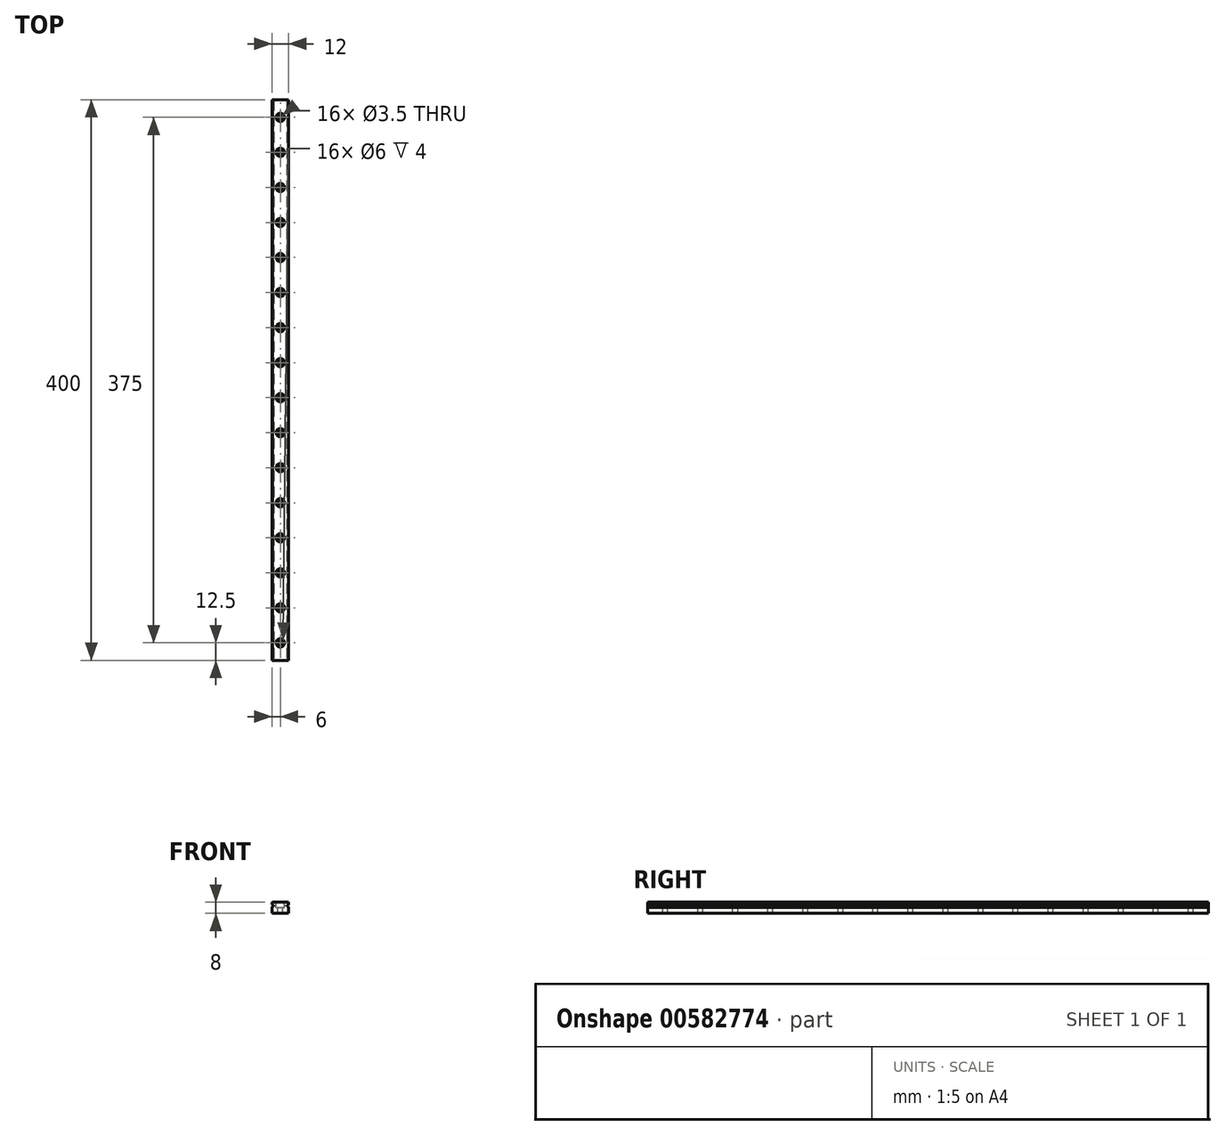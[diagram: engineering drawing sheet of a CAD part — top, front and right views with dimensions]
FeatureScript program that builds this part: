
annotation { "Feature Type Name" : "Feature", "Feature Type Description" : "" }
export const myFeature = defineFeature(function(context is Context, id is Id, definition is map)
    precondition{}
    {
        {
            var Q0;
            Q0=qCreatedBy(makeId("Front.planeOp"),FACE);
            var sketch = newSketch(context, id + "F0", { "sketchPlane" : qUnion([Q0])});
            skLineSegment(sketch, "E0.bottom", {"start": v(5.7, 3) * mm, "end": v(-5.7, 3) * mm});
            skLineSegment(sketch, "E0.top", {"start": v(5.7, -3) * mm, "end": v(-5.7, -3) * mm});
            skLineSegment(sketch, "E0.left", {"start": v(6, 2.7) * mm, "end": v(6, 1.45) * mm});
            skLineSegment(sketch, "E0.right", {"start": v(-6, 2.7) * mm, "end": v(-6, 1.45) * mm});
            skPoint(sketch, "E0.middle", {"position": v(0, 0) * mm});
            skLineSegment(sketch, "E1", {"start": v(-5.3, 0.08) * mm, "end": v(-4.69, 0.08) * mm});
            skLineSegment(sketch, "E2", {"start": v(-5.3, 0.72) * mm, "end": v(-4.69, 0.72) * mm});
            skLineSegment(sketch, "E3", {"start": v(-4.69, 0.72) * mm, "end": v(-4.69, 0.08) * mm});
            skArc(sketch, "E4", {"start": v(-5.3, 0.72) * mm, "mid": v(-5.56, 1.17) * mm, "end": v(-6, 1.45) * mm});
            skArc(sketch, "E5.trimOffspring", {"start": v(-6, -0.67) * mm, "mid": v(-5.56, -0.38) * mm, "end": v(-5.3, 0.08) * mm});
            skLineSegment(sketch, "E6.trimOffspring", {"start": v(-6, -0.67) * mm, "end": v(-6, -5) * mm});
            skLineSegment(sketch, "E7.MirrorCS", {"start": v(4.69, 0.72) * mm, "end": v(4.69, 0.08) * mm});
            skLineSegment(sketch, "E8.MirrorCS", {"start": v(5.3, 0.72) * mm, "end": v(4.69, 0.72) * mm});
            skLineSegment(sketch, "E9.MirrorCS", {"start": v(5.3, 0.08) * mm, "end": v(4.69, 0.08) * mm});
            skArc(sketch, "E10.MirrorCS", {"start": v(5.3, 0.72) * mm, "mid": v(5.56, 1.17) * mm, "end": v(6, 1.45) * mm});
            skArc(sketch, "E11.MirrorCS", {"start": v(6, -0.67) * mm, "mid": v(5.56, -0.38) * mm, "end": v(5.3, 0.08) * mm});
            skLineSegment(sketch, "E12.trimOffspring", {"start": v(6, -0.67) * mm, "end": v(6, -5) * mm});
            skPoint(sketch, "E13.orphan", {"position": v(-6, -3) * mm});
            skLineSegment(sketch, "E14.MirrorCS", {"start": v(-5.7, 3) * mm, "end": v(-6, 2.7) * mm});
            skPoint(sketch, "E15.MirrorP", {"position": v(-6, 3) * mm});
            skPoint(sketch, "E16.MirrorP", {"position": v(-5.7, -2.7) * mm});
            skLineSegment(sketch, "E17.MirrorCS", {"start": v(5.7, 3) * mm, "end": v(6, 2.7) * mm});
            skLineSegment(sketch, "E18.MirrorCS", {"start": v(5.7, -3) * mm, "end": v(6, -2.7) * mm});
            skPoint(sketch, "E19.MirrorP", {"position": v(6, -3) * mm});
            skPoint(sketch, "E20.MirrorP", {"position": v(5.7, -2.7) * mm});
            skPoint(sketch, "E21.orphan", {"position": v(6, 3) * mm});
            skLineSegment(sketch, "E22.0", {"start": v(6, -5) * mm, "end": v(-6, -5) * mm});
            skPoint(sketch, "E23.MirrorCS.end.orphan", {"position": v(6, -2.7) * mm});
            skPoint(sketch, "E23.MirrorCS.start.orphan", {"position": v(5.7, -3) * mm});
            skPoint(sketch, "E24.end.orphan", {"position": v(-6, -2.7) * mm});
            skSolve(sketch);
        }
        {
            var Q0;
            Q0=makeQuery(id+"F0.imprint","IMPRINT",FACE,{"disambiguationData":[TD([[makeQuery(id+"F0.imprint","IMPRINT",EDGE,{"derivedFrom":sQuery(id+"F0.wireOp",EDGE,"E0.bottom")}),1.0]])]});
            extrude(context, id + "F1", {"entities" : qUnion([Q0]), "depth" : -400 * mm, "offsetDistance" : 25 * mm});
        }
        {
            var Q0;
            Q0=makeQuery(id+"F1.opExtrude","SWEPT_FACE",FACE,{"disambiguationData":[OSD([sQuery(id+"F0.wireOp",EDGE,"E0.bottom")])]});
            var sketch = newSketch(context, id + "F2", { "sketchPlane" : qUnion([Q0])});
            skLineSegment(sketch, "E25", {"start": v(0, 0) * mm, "end": v(0, 409.67) * mm});
            skLineSegment(sketch, "E26", {"start": v(-11.77, 0) * mm, "end": v(-11.77, 12.5) * mm});
            skLineSegment(sketch, "E27", {"start": v(-11.77, 12.5) * mm, "end": v(13.91, 12.5) * mm});
            skCircle(sketch, "E28", {"center": v(0, 12.5) * mm, "radius": 0.73 * mm});
            skCircle(sketch, "E29.1.0.0", {"center": v(0, 37.5) * mm, "radius": 0.73 * mm});
            skCircle(sketch, "E29.2.0.0", {"center": v(0, 62.5) * mm, "radius": 0.73 * mm});
            skCircle(sketch, "E29.3.0.0", {"center": v(0, 87.5) * mm, "radius": 0.73 * mm});
            skCircle(sketch, "E29.4.0.0", {"center": v(0, 112.5) * mm, "radius": 0.73 * mm});
            skCircle(sketch, "E29.5.0.0", {"center": v(0, 137.5) * mm, "radius": 0.73 * mm});
            skCircle(sketch, "E29.6.0.0", {"center": v(0, 162.5) * mm, "radius": 0.73 * mm});
            skCircle(sketch, "E29.7.0.0", {"center": v(0, 187.5) * mm, "radius": 0.73 * mm});
            skCircle(sketch, "E29.8.0.0", {"center": v(0, 212.5) * mm, "radius": 0.73 * mm});
            skCircle(sketch, "E29.9.0.0", {"center": v(0, 237.5) * mm, "radius": 0.73 * mm});
            skCircle(sketch, "E29.10.0.0", {"center": v(0, 262.5) * mm, "radius": 0.73 * mm});
            skCircle(sketch, "E29.11.0.0", {"center": v(0, 287.5) * mm, "radius": 0.73 * mm});
            skCircle(sketch, "E29.12.0.0", {"center": v(0, 312.5) * mm, "radius": 0.73 * mm});
            skCircle(sketch, "E29.13.0.0", {"center": v(0, 337.5) * mm, "radius": 0.73 * mm});
            skCircle(sketch, "E29.14.0.0", {"center": v(0, 362.5) * mm, "radius": 0.73 * mm});
            skLineSegment(sketch, "E29.direction1", {"start": v(0, 12.5) * mm, "end": v(0, 37.5) * mm, "construction": true});
            skCircle(sketch, "E30.0.15.0", {"center": v(0, 387.5) * mm, "radius": 0.73 * mm});
            skSolve(sketch);
        }
        {
            var Q0;
            Q0=sQuery(id+"F2.wireOp",VERTEX,"E28.center");
            var Q1;
            Q1=sQuery(id+"F2.wireOp",VERTEX,"E29.1.0.0.center");
            var Q2;
            Q2=sQuery(id+"F2.wireOp",VERTEX,"E29.2.0.0.center");
            var Q3;
            Q3=sQuery(id+"F2.wireOp",VERTEX,"E29.3.0.0.center");
            var Q4;
            Q4=sQuery(id+"F2.wireOp",VERTEX,"E29.4.0.0.center");
            var Q5;
            Q5=sQuery(id+"F2.wireOp",VERTEX,"E29.5.0.0.center");
            var Q6;
            Q6=sQuery(id+"F2.wireOp",VERTEX,"E29.6.0.0.center");
            var Q7;
            Q7=sQuery(id+"F2.wireOp",VERTEX,"E29.7.0.0.center");
            var Q8;
            Q8=sQuery(id+"F2.wireOp",VERTEX,"E29.8.0.0.center");
            var Q9;
            Q9=sQuery(id+"F2.wireOp",VERTEX,"E29.9.0.0.center");
            var Q10;
            Q10=sQuery(id+"F2.wireOp",VERTEX,"E29.10.0.0.center");
            var Q11;
            Q11=sQuery(id+"F2.wireOp",VERTEX,"E29.11.0.0.center");
            var Q12;
            Q12=sQuery(id+"F2.wireOp",VERTEX,"E29.12.0.0.center");
            var Q13;
            Q13=sQuery(id+"F2.wireOp",VERTEX,"E29.13.0.0.center");
            var Q14;
            Q14=sQuery(id+"F2.wireOp",VERTEX,"E29.14.0.0.center");
            var Q15;
            Q15=sQuery(id+"F2.wireOp",VERTEX,"E30.0.15.0.center");
            var Q16;
            Q16=makeQuery(id+"F1.opExtrude","SWEPT_BODY",BODY,{"disambiguationData":[OSD([sQuery(id+"F0.wireOp",EDGE,"E0.bottom"),sQuery(id+"F0.wireOp",EDGE,"E0.top"),sQuery(id+"F0.wireOp",EDGE,"E0.left"),sQuery(id+"F0.wireOp",EDGE,"E0.right"),sQuery(id+"F0.wireOp",EDGE,"E1"),sQuery(id+"F0.wireOp",EDGE,"E2"),sQuery(id+"F0.wireOp",EDGE,"E3"),sQuery(id+"F0.wireOp",EDGE,"E4"),sQuery(id+"F0.wireOp",EDGE,"E5.trimOffspring"),sQuery(id+"F0.wireOp",EDGE,"E6.trimOffspring"),sQuery(id+"F0.wireOp",EDGE,"E7.MirrorCS"),sQuery(id+"F0.wireOp",EDGE,"E8.MirrorCS"),sQuery(id+"F0.wireOp",EDGE,"E9.MirrorCS"),sQuery(id+"F0.wireOp",EDGE,"E10.MirrorCS"),sQuery(id+"F0.wireOp",EDGE,"E11.MirrorCS"),sQuery(id+"F0.wireOp",EDGE,"E12.trimOffspring"),sQuery(id+"F0.wireOp",EDGE,"E24"),sQuery(id+"F0.wireOp",EDGE,"E14.MirrorCS"),sQuery(id+"F0.wireOp",EDGE,"E17.MirrorCS"),sQuery(id+"F0.wireOp",EDGE,"E18.MirrorCS")])]});
            hole(context, id + "F3", {"style" : HoleStyle.C_BORE, "endStyle" : HoleEndStyle.THROUGH, "holeDiameter" : 3.5 * mm, "cBoreDiameter" : 6 * mm, "cBoreDepth" : 4 * mm, "majorDiameter" : 5 * mm, "isTappedThrough" : true, "tappedDepth" : 12 * mm, "tapClearance" : 3, "startFromSketch" : true, "locations" : qUnion([Q0, Q1, Q2, Q3, Q4, Q5, Q6, Q7, Q8, Q9, Q10, Q11, Q12, Q13, Q14, Q15]), "scope" : qUnion([Q16])});
        }
    });
